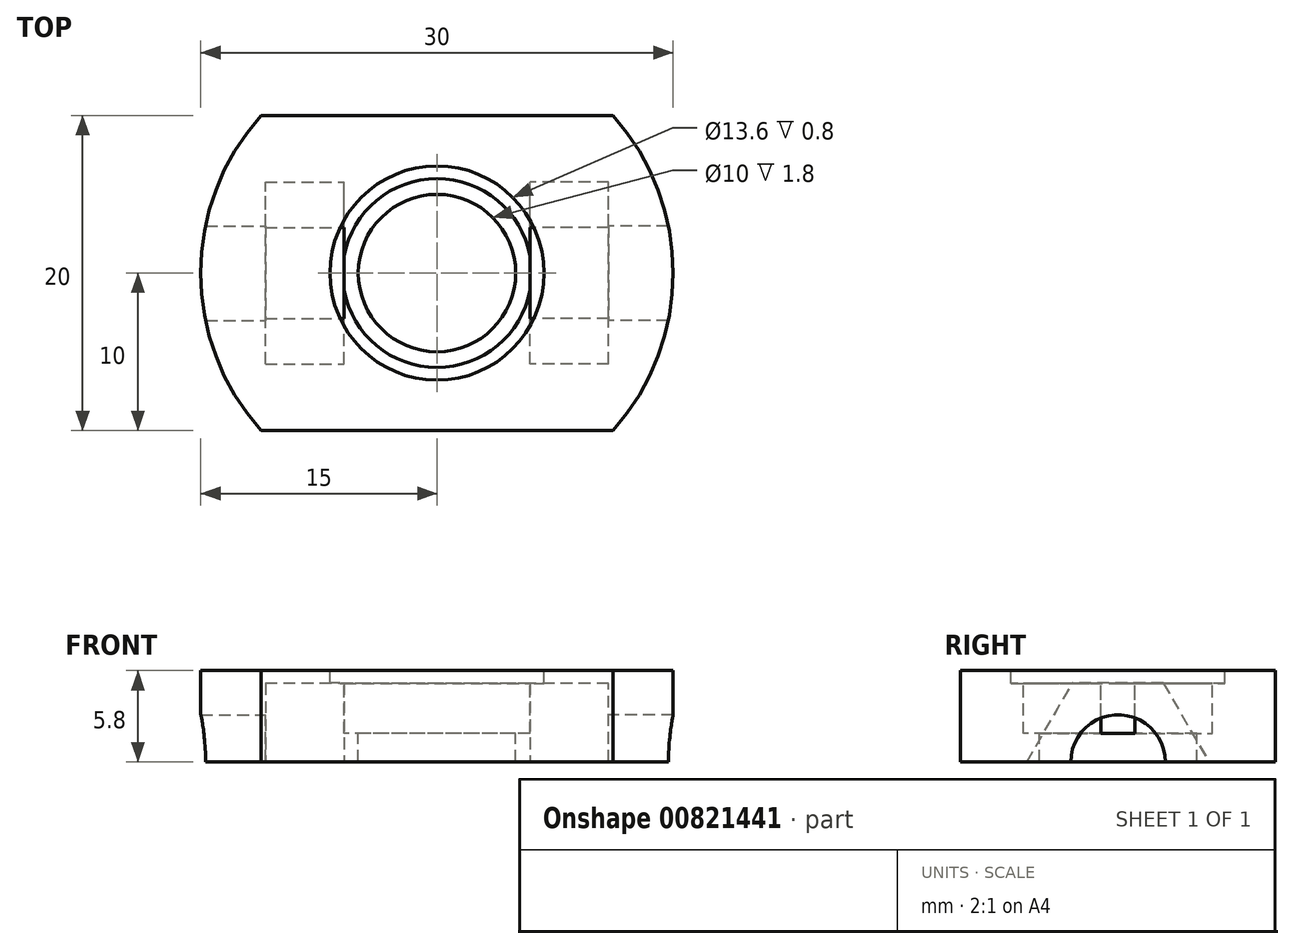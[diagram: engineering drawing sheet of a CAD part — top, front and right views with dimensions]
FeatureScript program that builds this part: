
annotation { "Feature Type Name" : "Feature", "Feature Type Description" : "" }
export const myFeature = defineFeature(function(context is Context, id is Id, definition is map)
    precondition{}
    {
        {
            var Q0;
            Q0=qCreatedBy(makeId("Top.planeOp"),FACE);
            var sketch = newSketch(context, id + "F0", { "sketchPlane" : qUnion([Q0])});
            skCircle(sketch, "E0", {"center": v(0, 0) * mm, "radius": 15 * mm});
            skSolve(sketch);
        }
        {
            var Q0;
            Q0 = qSketchRegion(id + "F0", true);
            extrude(context, id + "F1", {"entities" : qUnion([Q0]), "depth" : 5.8 * mm, "offsetDistance" : 25 * mm});
        }
        {
            var Q0;
            Q0=makeQuery(id+"F1.opExtrude","CAP_FACE",FACE,{"disambiguationData":[OSD([sQuery(id+"F0.wireOp",EDGE,"E0")])],"isStart":false});
            var sketch = newSketch(context, id + "F2", { "sketchPlane" : qUnion([Q0])});
            skCircle(sketch, "E1", {"center": v(0, 0) * mm, "radius": 6.8 * mm});
            skSolve(sketch);
        }
        {
            var Q0;
            Q0 = qSketchRegion(id + "F2", true);
            extrude(context, id + "F3", {"entities" : qUnion([Q0]), "operationType" : NewBodyOperationType.REMOVE, "oppositeDirection" : true, "depth" : 0.8 * mm, "offsetDistance" : 25 * mm});
        }
        {
            var Q0;
            Q0=makeQuery(id+"F3.boolean.opBoolean","COPY",FACE,{"derivedFrom":makeQuery(id+"F3.opExtrude","CAP_FACE",FACE,{"disambiguationData":[OSD([sQuery(id+"F2.wireOp",EDGE,"E1")])],"isStart":false})});
            var sketch = newSketch(context, id + "F4", { "sketchPlane" : qUnion([Q0])});
            skCircle(sketch, "E2", {"center": v(0, 0) * mm, "radius": 6 * mm});
            skSolve(sketch);
        }
        {
            var Q0;
            Q0 = qSketchRegion(id + "F4", true);
            extrude(context, id + "F5", {"entities" : qUnion([Q0]), "operationType" : NewBodyOperationType.REMOVE, "oppositeDirection" : true, "depth" : 3.2 * mm, "offsetDistance" : 25 * mm});
        }
        {
            var Q0;
            Q0=makeQuery(id+"F5.boolean.opBoolean","COPY",FACE,{"derivedFrom":makeQuery(id+"F5.opExtrude","CAP_FACE",FACE,{"disambiguationData":[OSD([sQuery(id+"F4.wireOp",EDGE,"E2")])],"isStart":false})});
            var sketch = newSketch(context, id + "F6", { "sketchPlane" : qUnion([Q0])});
            skCircle(sketch, "E3", {"center": v(0, 0) * mm, "radius": 5 * mm});
            skSolve(sketch);
        }
        {
            var Q0;
            Q0 = qSketchRegion(id + "F6", true);
            extrude(context, id + "F7", {"entities" : qUnion([Q0]), "operationType" : NewBodyOperationType.REMOVE, "endBound" : BoundingType.UP_TO_NEXT, "oppositeDirection" : true, "depth" : 25 * mm, "offsetDistance" : 25 * mm});
        }
        {
            var Q0;
            Q0=qCreatedBy(makeId("Right.planeOp"),FACE);
            cPlane(context, id + "F8", {"entities" : qUnion([Q0]), "cplaneType" : CPlaneType.OFFSET, "offset" : 5.9 * mm, "width" : 150 * mm, "height" : 150 * mm});
        }
        {
            var Q0;
            Q0=qCreatedBy(makeId("Right.planeOp"),FACE);
            cPlane(context, id + "F9", {"entities" : qUnion([Q0]), "cplaneType" : CPlaneType.OFFSET, "offset" : 5.9 * mm, "oppositeDirection" : true, "width" : 150 * mm, "height" : 150 * mm});
        }
        {
            var Q0;
            Q0=qCreatedBy(id+"F8.planeOp",FACE);
            var sketch = newSketch(context, id + "F10", { "sketchPlane" : qUnion([Q0])});
            skCircle(sketch, "E4.cCircle", {"center": v(0, 0) * mm, "radius": 5 * mm, "construction": true});
            skLineSegment(sketch, "E4.0", {"start": v(-2.89, 5) * mm, "end": v(2.89, 5) * mm});
            skLineSegment(sketch, "E4.1", {"start": v(2.89, 5) * mm, "end": v(5.77, 0) * mm});
            skLineSegment(sketch, "E4.2", {"start": v(5.77, 0) * mm, "end": v(2.89, -5) * mm});
            skLineSegment(sketch, "E4.3", {"start": v(2.89, -5) * mm, "end": v(-2.89, -5) * mm});
            skLineSegment(sketch, "E4.4", {"start": v(-2.89, -5) * mm, "end": v(-5.77, 0) * mm});
            skLineSegment(sketch, "E4.5", {"start": v(-5.77, 0) * mm, "end": v(-2.89, 5) * mm});
            skPoint(sketch, "E4.0.midPoint", {"position": v(0, 5) * mm});
            skSolve(sketch);
        }
        {
            var Q0;
            Q0 = qSketchRegion(id + "F10", true);
            extrude(context, id + "F11", {"entities" : qUnion([Q0]), "operationType" : NewBodyOperationType.REMOVE, "depth" : 5 * mm, "offsetDistance" : 25 * mm});
        }
        {
            var Q0;
            Q0=qCreatedBy(id+"F9.planeOp",FACE);
            var sketch = newSketch(context, id + "F12", { "sketchPlane" : qUnion([Q0])});
            skCircle(sketch, "E5.cCircle", {"center": v(0, 0) * mm, "radius": 5 * mm, "construction": true});
            skLineSegment(sketch, "E5.0", {"start": v(-2.89, 5) * mm, "end": v(2.89, 5) * mm});
            skLineSegment(sketch, "E5.1", {"start": v(2.89, 5) * mm, "end": v(5.78, 0) * mm});
            skLineSegment(sketch, "E5.2", {"start": v(5.78, 0) * mm, "end": v(2.89, -5) * mm});
            skLineSegment(sketch, "E5.3", {"start": v(2.89, -5) * mm, "end": v(-2.89, -5) * mm});
            skLineSegment(sketch, "E5.4", {"start": v(-2.89, -5) * mm, "end": v(-5.78, 0) * mm});
            skLineSegment(sketch, "E5.5", {"start": v(-5.78, 0) * mm, "end": v(-2.89, 5) * mm});
            skPoint(sketch, "E5.0.midPoint", {"position": v(0, 5) * mm});
            skSolve(sketch);
        }
        {
            var Q0;
            Q0 = qSketchRegion(id + "F12", true);
            extrude(context, id + "F13", {"entities" : qUnion([Q0]), "operationType" : NewBodyOperationType.REMOVE, "oppositeDirection" : true, "depth" : 5 * mm, "offsetDistance" : 25 * mm});
        }
        {
            var Q0;
            Q0=qCreatedBy(id+"F9.planeOp",FACE);
            var sketch = newSketch(context, id + "F14", { "sketchPlane" : qUnion([Q0])});
            skCircle(sketch, "E6", {"center": v(0, 0) * mm, "radius": 3 * mm});
            skSolve(sketch);
        }
        {
            var Q0;
            Q0 = qSketchRegion(id + "F14", true);
            extrude(context, id + "F15", {"entities" : qUnion([Q0]), "operationType" : NewBodyOperationType.REMOVE, "oppositeDirection" : true, "depth" : 25 * mm, "offsetDistance" : 25 * mm});
        }
        {
            var Q0;
            Q0=qCreatedBy(id+"F8.planeOp",FACE);
            var sketch = newSketch(context, id + "F16", { "sketchPlane" : qUnion([Q0])});
            skCircle(sketch, "E7", {"center": v(0, 0) * mm, "radius": 3 * mm});
            skSolve(sketch);
        }
        {
            var Q0;
            Q0 = qSketchRegion(id + "F16", true);
            extrude(context, id + "F17", {"entities" : qUnion([Q0]), "operationType" : NewBodyOperationType.REMOVE, "depth" : 25 * mm, "offsetDistance" : 25 * mm});
        }
        {
            var Q0;
            Q0=qCreatedBy(makeId("Top.planeOp"),FACE);
            var sketch = newSketch(context, id + "F18", { "sketchPlane" : qUnion([Q0])});
            skLineSegment(sketch, "E8.bottom", {"start": v(-12.5, 15) * mm, "end": v(12.5, 15) * mm});
            skLineSegment(sketch, "E8.top", {"start": v(-12.5, 10) * mm, "end": v(12.5, 10) * mm});
            skLineSegment(sketch, "E8.left", {"start": v(-12.5, 15) * mm, "end": v(-12.5, 10) * mm});
            skLineSegment(sketch, "E8.right", {"start": v(12.5, 15) * mm, "end": v(12.5, 10) * mm});
            skLineSegment(sketch, "E9.bottom", {"start": v(-12.5, -10) * mm, "end": v(12.5, -10) * mm});
            skLineSegment(sketch, "E9.top", {"start": v(-12.5, -15) * mm, "end": v(12.5, -15) * mm});
            skLineSegment(sketch, "E9.left", {"start": v(-12.5, -10) * mm, "end": v(-12.5, -15) * mm});
            skLineSegment(sketch, "E9.right", {"start": v(12.5, -10) * mm, "end": v(12.5, -15) * mm});
            skSolve(sketch);
        }
        {
            var Q0;
            Q0 = qSketchRegion(id + "F18", true);
            extrude(context, id + "F19", {"entities" : qUnion([Q0]), "operationType" : NewBodyOperationType.REMOVE, "endBound" : BoundingType.UP_TO_NEXT, "depth" : 25 * mm, "offsetDistance" : 25 * mm});
        }
    });
